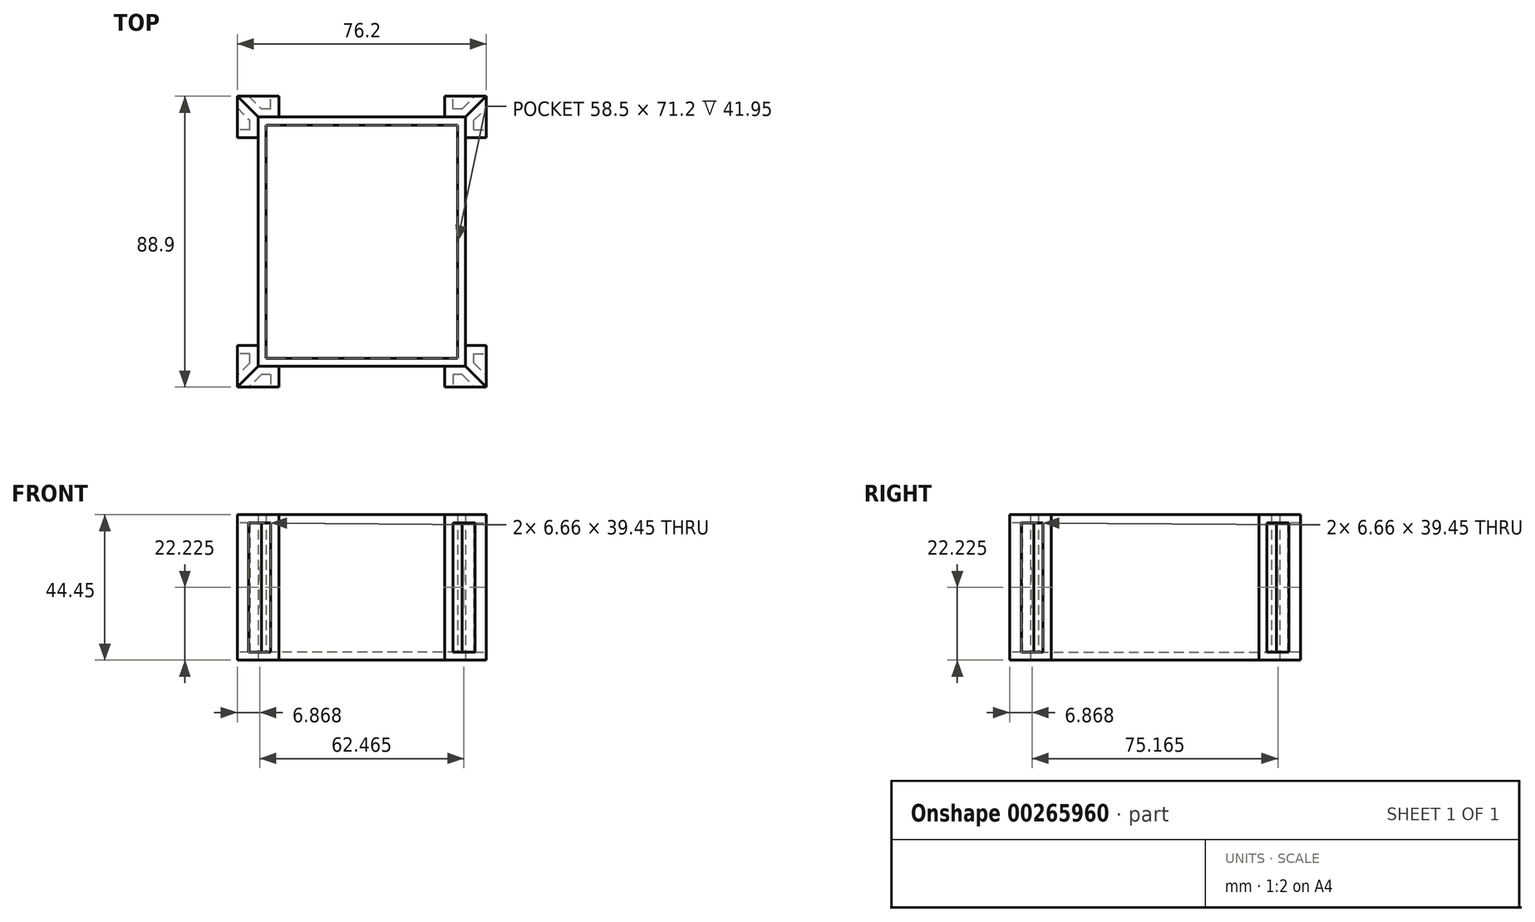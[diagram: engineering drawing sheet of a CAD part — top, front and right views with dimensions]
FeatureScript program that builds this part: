
annotation { "Feature Type Name" : "Feature", "Feature Type Description" : "" }
export const myFeature = defineFeature(function(context is Context, id is Id, definition is map)
    precondition{}
    {
        {
            var Q0;
            Q0=qCreatedBy(makeId("Top.planeOp"),FACE);
            var sketch = newSketch(context, id + "F0", { "sketchPlane" : qUnion([Q0])});
            skLineSegment(sketch, "E0.bottom", {"start": v(31.75, -38.1) * mm, "end": v(-31.75, -38.1) * mm});
            skLineSegment(sketch, "E0.top", {"start": v(31.75, 38.1) * mm, "end": v(-31.75, 38.1) * mm});
            skLineSegment(sketch, "E0.left", {"start": v(31.75, -38.1) * mm, "end": v(31.75, 38.1) * mm});
            skLineSegment(sketch, "E0.right", {"start": v(-31.75, -38.1) * mm, "end": v(-31.75, 38.1) * mm});
            skPoint(sketch, "E0.middle", {"position": v(0, 0) * mm});
            skPoint(sketch, "E1.middle", {"position": v(-31.75, 38.1) * mm});
            skPoint(sketch, "E2.middle", {"position": v(31.75, 38.1) * mm});
            skPoint(sketch, "E3.middle", {"position": v(31.75, -38.1) * mm});
            skPoint(sketch, "E4.middle", {"position": v(-31.75, -38.1) * mm});
            skLineSegment(sketch, "E5.bottom", {"start": v(-31.75, 31.75) * mm, "end": v(-38.1, 31.75) * mm});
            skLineSegment(sketch, "E5.top", {"start": v(-25.4, 44.45) * mm, "end": v(-38.1, 44.45) * mm});
            skLineSegment(sketch, "E5.left", {"start": v(-25.4, 38.1) * mm, "end": v(-25.4, 44.45) * mm});
            skLineSegment(sketch, "E5.right", {"start": v(-38.1, 31.75) * mm, "end": v(-38.1, 44.45) * mm});
            skPoint(sketch, "E6.orphan", {"position": v(-25.4, 31.75) * mm});
            skLineSegment(sketch, "E7.MirrorCS", {"start": v(25.4, 44.45) * mm, "end": v(38.1, 44.45) * mm});
            skLineSegment(sketch, "E8.MirrorCS", {"start": v(25.4, 38.1) * mm, "end": v(25.4, 44.45) * mm});
            skLineSegment(sketch, "E9.MirrorCS", {"start": v(38.1, 31.75) * mm, "end": v(38.1, 44.45) * mm});
            skLineSegment(sketch, "E10.MirrorCS", {"start": v(31.75, 31.75) * mm, "end": v(38.1, 31.75) * mm});
            skLineSegment(sketch, "E11.MirrorCS", {"start": v(38.1, -31.75) * mm, "end": v(38.1, -44.45) * mm});
            skLineSegment(sketch, "E12.MirrorCS", {"start": v(25.4, -44.45) * mm, "end": v(38.1, -44.45) * mm});
            skLineSegment(sketch, "E13.MirrorCS", {"start": v(25.4, -38.1) * mm, "end": v(25.4, -44.45) * mm});
            skLineSegment(sketch, "E14.MirrorCS", {"start": v(31.75, -31.75) * mm, "end": v(38.1, -31.75) * mm});
            skLineSegment(sketch, "E15.MirrorCS", {"start": v(-38.1, -31.75) * mm, "end": v(-38.1, -44.45) * mm});
            skLineSegment(sketch, "E16.MirrorCS", {"start": v(-31.75, -31.75) * mm, "end": v(-38.1, -31.75) * mm});
            skLineSegment(sketch, "E17.MirrorCS", {"start": v(-25.4, -44.45) * mm, "end": v(-38.1, -44.45) * mm});
            skLineSegment(sketch, "E18.MirrorCS", {"start": v(-25.4, -38.1) * mm, "end": v(-25.4, -44.45) * mm});
            skLineSegment(sketch, "E19", {"start": v(-38.1, 44.45) * mm, "end": v(-31.75, 38.1) * mm});
            skLineSegment(sketch, "E20", {"start": v(31.75, 38.1) * mm, "end": v(38.1, 44.45) * mm});
            skLineSegment(sketch, "E21", {"start": v(31.75, -38.1) * mm, "end": v(38.1, -44.45) * mm});
            skLineSegment(sketch, "E22", {"start": v(-31.75, -38.1) * mm, "end": v(-38.1, -44.45) * mm});
            skSolve(sketch);
        }
        {
            var Q0;
            Q0=makeQuery(id+"F0.imprint","IMPRINT",FACE,{"disambiguationData":[TD([[makeQuery(id+"F0.imprint","IMPRINT",EDGE,{"derivedFrom":sQuery(id+"F0.wireOp",EDGE,"E0.bottom")}),-1.0]])]});
            extrude(context, id + "F1", {"entities" : qUnion([Q0]), "depth" : 44.45 * mm});
        }
        {
            var Q0;
            Q0=makeQuery(id+"F1.opExtrude","CAP_FACE",FACE,{"disambiguationData":[OSD([sQuery(id+"F0.wireOp",EDGE,"E0.bottom"),sQuery(id+"F0.wireOp",EDGE,"E0.top"),sQuery(id+"F0.wireOp",EDGE,"E0.left"),sQuery(id+"F0.wireOp",EDGE,"E0.right")])],"isStart":false});
            shell(context, id + "F2", {"entities" : qUnion([Q0]), "thickness" : 2.5 * mm});
        }
        {
            var Q0;
            Q0=makeQuery(id+"F0.imprint","IMPRINT",FACE,{"disambiguationData":[TD([[makeQuery(id+"F0.imprint","IMPRINT",EDGE,{"derivedFrom":sQuery(id+"F0.wireOp",EDGE,"E7.MirrorCS")}),-1.0]])]});
            var Q1;
            Q1=makeQuery(id+"F0.imprint","IMPRINT",FACE,{"disambiguationData":[TD([[makeQuery(id+"F0.imprint","IMPRINT",EDGE,{"derivedFrom":sQuery(id+"F0.wireOp",EDGE,"E11.MirrorCS")}),-1.0]])]});
            var Q2;
            Q2=makeQuery(id+"F0.imprint","IMPRINT",FACE,{"disambiguationData":[TD([[makeQuery(id+"F0.imprint","IMPRINT",EDGE,{"derivedFrom":sQuery(id+"F0.wireOp",EDGE,"E15.MirrorCS")}),1.0]])]});
            var Q3;
            Q3=makeQuery(id+"F0.imprint","IMPRINT",FACE,{"disambiguationData":[TD([[makeQuery(id+"F0.imprint","IMPRINT",EDGE,{"derivedFrom":sQuery(id+"F0.wireOp",EDGE,"E5.top")}),1.0]])]});
            extrude(context, id + "F3", {"entities" : qUnion([Q0, Q1, Q2, Q3]), "depth" : 44.45 * mm});
        }
        {
            var Q0;
            {var subQ2=sQuery(id+"F0.wireOp",EDGE,"E5.bottom");Q0=makeQuery(id+"F0.imprint","IMPRINT",FACE,{"disambiguationData":[TD([[makeQuery(id+"F0.imprint","IMPRINT",EDGE,{"derivedFrom":subQ2}),-1.0]])]});}
            var Q1;
            Q1=makeQuery(id+"F0.imprint","IMPRINT",FACE,{"disambiguationData":[TD([[makeQuery(id+"F0.imprint","IMPRINT",EDGE,{"derivedFrom":sQuery(id+"F0.wireOp",EDGE,"E9.MirrorCS")}),1.0]])]});
            var Q2;
            Q2=makeQuery(id+"F0.imprint","IMPRINT",FACE,{"disambiguationData":[TD([[makeQuery(id+"F0.imprint","IMPRINT",EDGE,{"derivedFrom":sQuery(id+"F0.wireOp",EDGE,"E12.MirrorCS")}),1.0]])]});
            var Q3;
            Q3=makeQuery(id+"F0.imprint","IMPRINT",FACE,{"disambiguationData":[TD([[makeQuery(id+"F0.imprint","IMPRINT",EDGE,{"derivedFrom":sQuery(id+"F0.wireOp",EDGE,"E17.MirrorCS")}),-1.0]])]});
            extrude(context, id + "F4", {"entities" : qUnion([Q0, Q1, Q2, Q3]), "depth" : 44.45 * mm});
        }
        {
            var Q0;
            Q0=makeQuery(id+"F3.opExtrude","SWEPT_FACE",FACE,{"disambiguationData":[OSD([sQuery(id+"F0.wireOp",EDGE,"E11.MirrorCS")])]});
            var Q1;
            Q1=makeQuery(id+"F4.opExtrude","SWEPT_FACE",FACE,{"disambiguationData":[OSD([sQuery(id+"F0.wireOp",EDGE,"E12.MirrorCS")])]});
            shell(context, id + "F5", {"entities" : qUnion([Q0, Q1]), "thickness" : 2.5 * mm});
        }
        {
            var Q0;
            Q0=makeQuery(id+"F3.opExtrude","SWEPT_FACE",FACE,{"disambiguationData":[OSD([sQuery(id+"F0.wireOp",EDGE,"E7.MirrorCS")])]});
            var Q1;
            Q1=makeQuery(id+"F4.opExtrude","SWEPT_FACE",FACE,{"disambiguationData":[OSD([sQuery(id+"F0.wireOp",EDGE,"E9.MirrorCS")])]});
            var Q2;
            Q2=makeQuery(id+"F4.opExtrude","SWEPT_FACE",FACE,{"disambiguationData":[OSD([sQuery(id+"F0.wireOp",EDGE,"E5.right")])]});
            var Q3;
            Q3=makeQuery(id+"F3.opExtrude","SWEPT_FACE",FACE,{"disambiguationData":[OSD([sQuery(id+"F0.wireOp",EDGE,"E5.top")])]});
            var Q4;
            Q4=makeQuery(id+"F4.opExtrude","SWEPT_FACE",FACE,{"disambiguationData":[OSD([sQuery(id+"F0.wireOp",EDGE,"E17.MirrorCS")])]});
            var Q5;
            Q5=makeQuery(id+"F3.opExtrude","SWEPT_FACE",FACE,{"disambiguationData":[OSD([sQuery(id+"F0.wireOp",EDGE,"E15.MirrorCS")])]});
            shell(context, id + "F6", {"entities" : qUnion([Q0, Q1, Q2, Q3, Q4, Q5]), "thickness" : 2.5 * mm});
        }
    });
